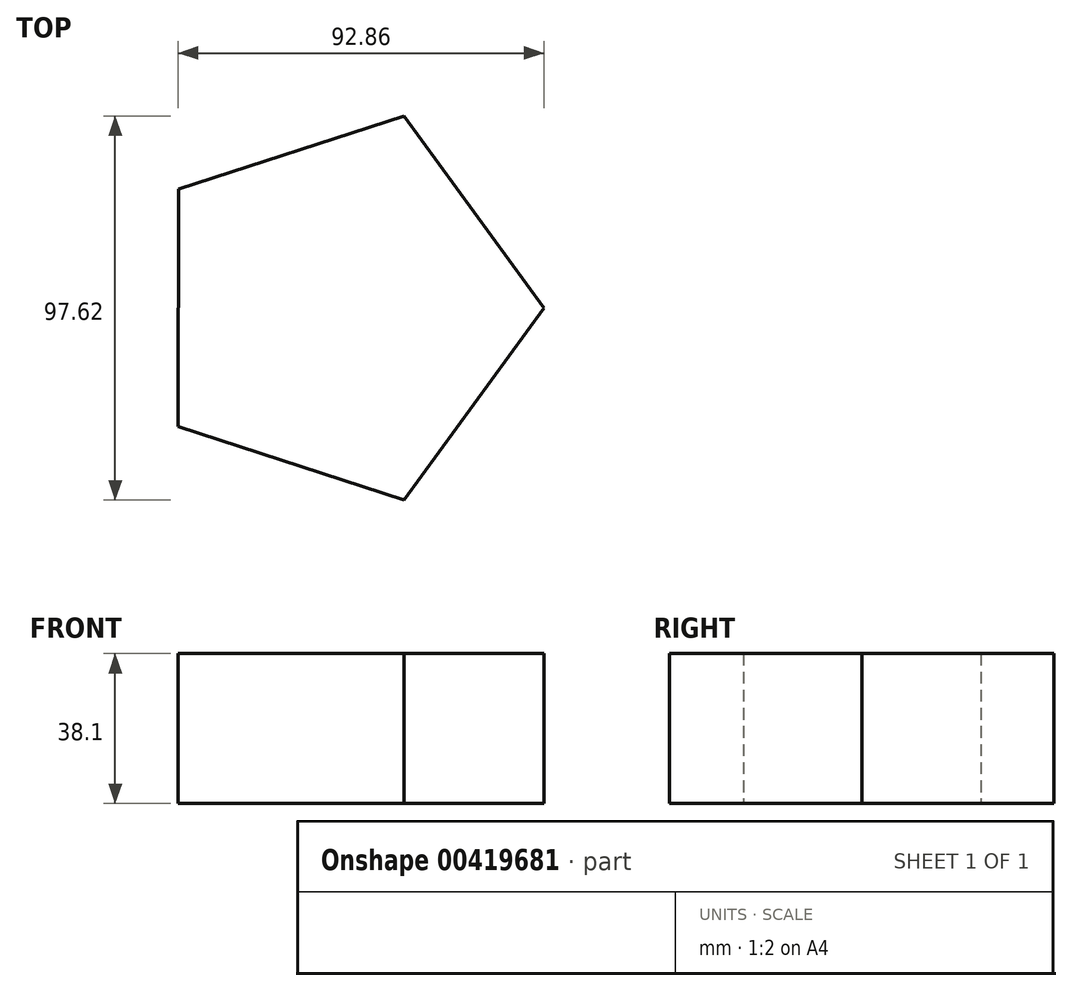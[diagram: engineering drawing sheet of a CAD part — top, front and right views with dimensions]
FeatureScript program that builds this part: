
annotation { "Feature Type Name" : "Feature", "Feature Type Description" : "" }
export const myFeature = defineFeature(function(context is Context, id is Id, definition is map)
    precondition{}
    {
        {
            var Q0;
            Q0=qCreatedBy(makeId("Top.planeOp"),FACE);
            var sketch = newSketch(context, id + "F0", { "sketchPlane" : qUnion([Q0])});
            skCircle(sketch, "E0.cCircle", {"center": v(-27.98, 16.4) * mm, "radius": 41.52 * mm, "construction": true});
            skLineSegment(sketch, "E0.0", {"start": v(23.34, 16.38) * mm, "end": v(-12.15, -32.41) * mm});
            skLineSegment(sketch, "E0.1", {"start": v(-12.15, -32.41) * mm, "end": v(-69.52, -13.74) * mm});
            skLineSegment(sketch, "E0.2", {"start": v(-69.52, -13.74) * mm, "end": v(-69.5, 46.6) * mm});
            skLineSegment(sketch, "E0.3", {"start": v(-69.5, 46.6) * mm, "end": v(-12.1, 65.21) * mm});
            skLineSegment(sketch, "E0.4", {"start": v(-12.1, 65.21) * mm, "end": v(23.34, 16.38) * mm});
            skPoint(sketch, "E0.0.midPoint", {"position": v(5.6, -8.01) * mm});
            skSolve(sketch);
        }
        {
            var Q0;
            Q0 = qSketchRegion(id + "F0", true);
            extrude(context, id + "F1", {"entities" : qUnion([Q0]), "depth" : 38.1 * mm});
        }
    });
